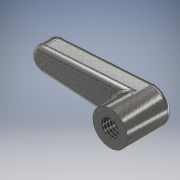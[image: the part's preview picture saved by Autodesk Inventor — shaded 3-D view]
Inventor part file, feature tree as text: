
AUTODESK INVENTOR PART (.ipt)
format: ipt  version: 2017 (Build 210142000, 142)  size: 210,944 bytes
history: native  units: mm
features: extrude x3, sketch x3, thread x1, fillet x1
ambient origin geometry x8: Origin, YZ Plane, XZ Plane, XY Plane, X Axis, Y Axis, Z Axis, Center Point
bodies: Body1 (feature_tree)
feature tree (8):
  extrude  "Extrusion3"  Depth=4.0mm TaperAngle=0.0deg
  extrude  "Extrusion4"  Depth=4.0mm TaperAngle=0.0deg
  extrude  "Extrusion5"  Depth=4.0mm TaperAngle=0.0deg
  thread  "Thread1"  [1 undecoded]
  fillet  "Fillet3"  Radius=1.0mm
  sketch  "Sketch3"  dims[d23=6.0mm d24=4.0mm d25=0.0mm]
  sketch  "Sketch4"  dims[d26=2.0mm d27=4.0mm d28=0.0mm]
  sketch  "Sketch5"  dims[d29=3.0mm d30=4.0mm d31=0.0mm d32=10.0mm d33=0.0mm d34=1.0mm d35=0.0mm d36=6.0mm d37=1.248376mm d38=2.994158mm d39=2.994158mm d40=5.988315mm d41=2.994158mm d42=2.994158mm d43=3.99221mm d44=1.996105mm d45=0.0mm d46=0.0mm]
note: 1 required parameter value undecoded (feature->parameter linkage not recoverable at this tier; creation-order binding heuristic only, values carry confidence <= 0.55)
